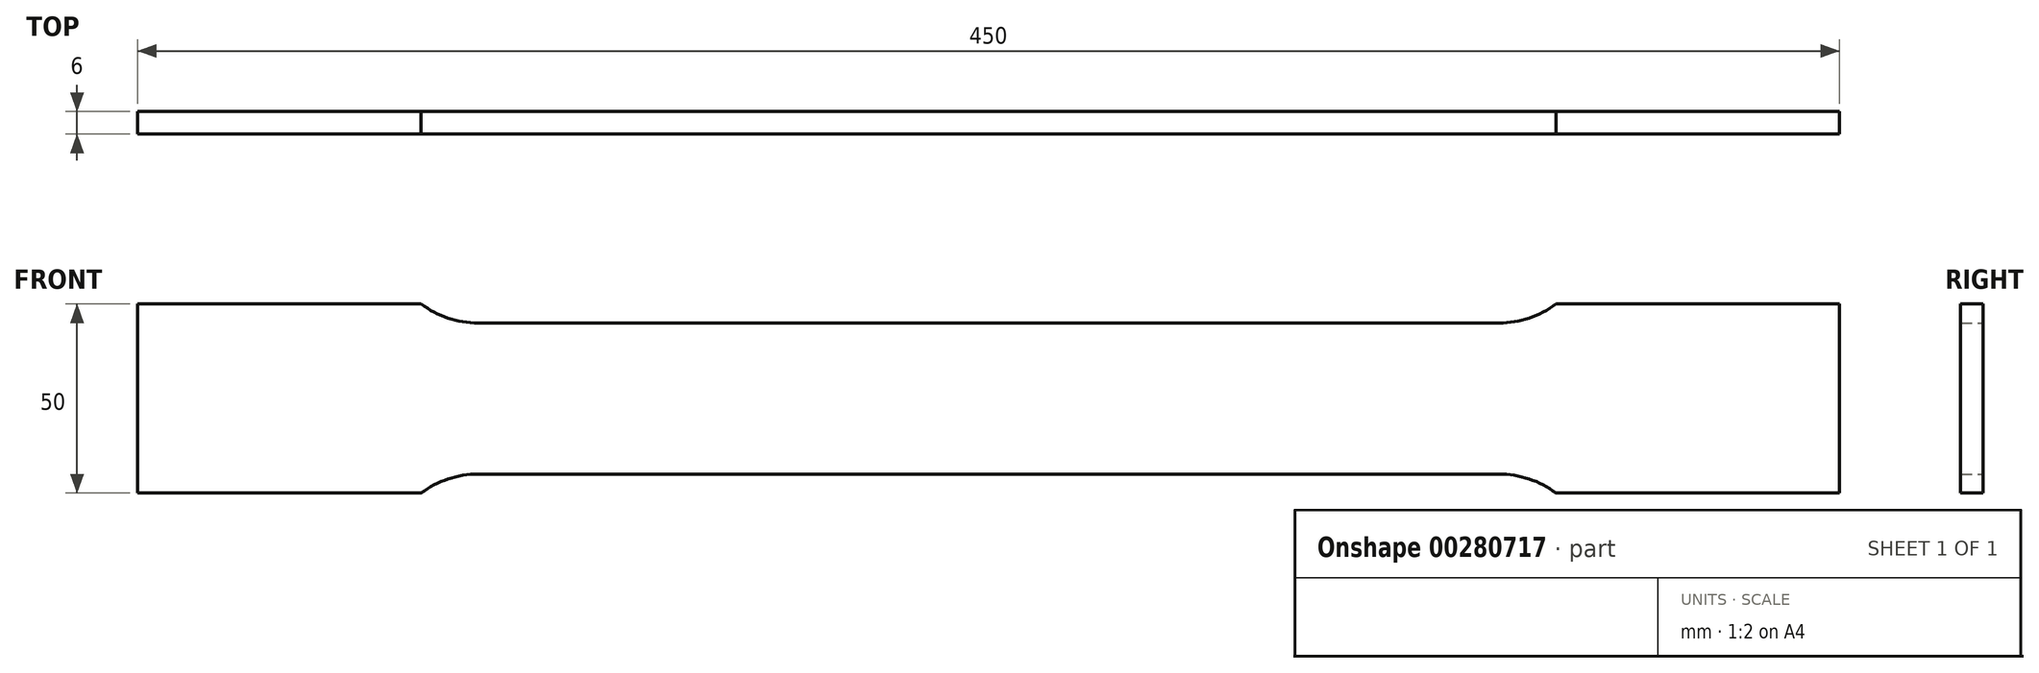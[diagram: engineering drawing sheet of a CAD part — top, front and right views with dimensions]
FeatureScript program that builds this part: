
annotation { "Feature Type Name" : "Feature", "Feature Type Description" : "" }
export const myFeature = defineFeature(function(context is Context, id is Id, definition is map)
    precondition{}
    {
        {
            var Q0;
            Q0=qCreatedBy(makeId("Front.planeOp"),FACE);
            var sketch = newSketch(context, id + "F0", { "sketchPlane" : qUnion([Q0])});
            skLineSegment(sketch, "E0", {"start": v(0, 20) * mm, "end": v(135, 20) * mm});
            skArc(sketch, "E1", {"start": v(135, 20) * mm, "mid": v(142.9, 21.28) * mm, "end": v(150, 25) * mm});
            skLineSegment(sketch, "E2", {"start": v(150, 25) * mm, "end": v(225, 25) * mm});
            skLineSegment(sketch, "E3.MirrorCS", {"start": v(0, -20) * mm, "end": v(135, -20) * mm});
            skLineSegment(sketch, "E4.MirrorCS", {"start": v(150, -25) * mm, "end": v(225, -25) * mm});
            skArc(sketch, "E5.MirrorCS", {"start": v(135, -20) * mm, "mid": v(142.9, -21.28) * mm, "end": v(150, -25) * mm});
            skLineSegment(sketch, "E6.MirrorCS", {"start": v(-150, 25) * mm, "end": v(-225, 25) * mm});
            skLineSegment(sketch, "E7.MirrorCS", {"start": v(-150, -25) * mm, "end": v(-225, -25) * mm});
            skArc(sketch, "E8.MirrorCS", {"start": v(-135, -20) * mm, "mid": v(-142.9, -21.28) * mm, "end": v(-150, -25) * mm});
            skLineSegment(sketch, "E9.MirrorCS", {"start": v(0, -20) * mm, "end": v(-135, -20) * mm});
            skLineSegment(sketch, "E10.MirrorCS", {"start": v(0, 20) * mm, "end": v(-135, 20) * mm});
            skArc(sketch, "E11.MirrorCS", {"start": v(-135, 20) * mm, "mid": v(-142.9, 21.28) * mm, "end": v(-150, 25) * mm});
            skLineSegment(sketch, "E12", {"start": v(-225, 25) * mm, "end": v(-225, -25) * mm});
            skLineSegment(sketch, "E13", {"start": v(225, 25) * mm, "end": v(225, -25) * mm});
            skSolve(sketch);
        }
        {
            var Q0;
            Q0 = qSketchRegion(id + "F0", true);
            extrude(context, id + "F1", {"entities" : qUnion([Q0]), "depth" : 6 * mm});
        }
    });
